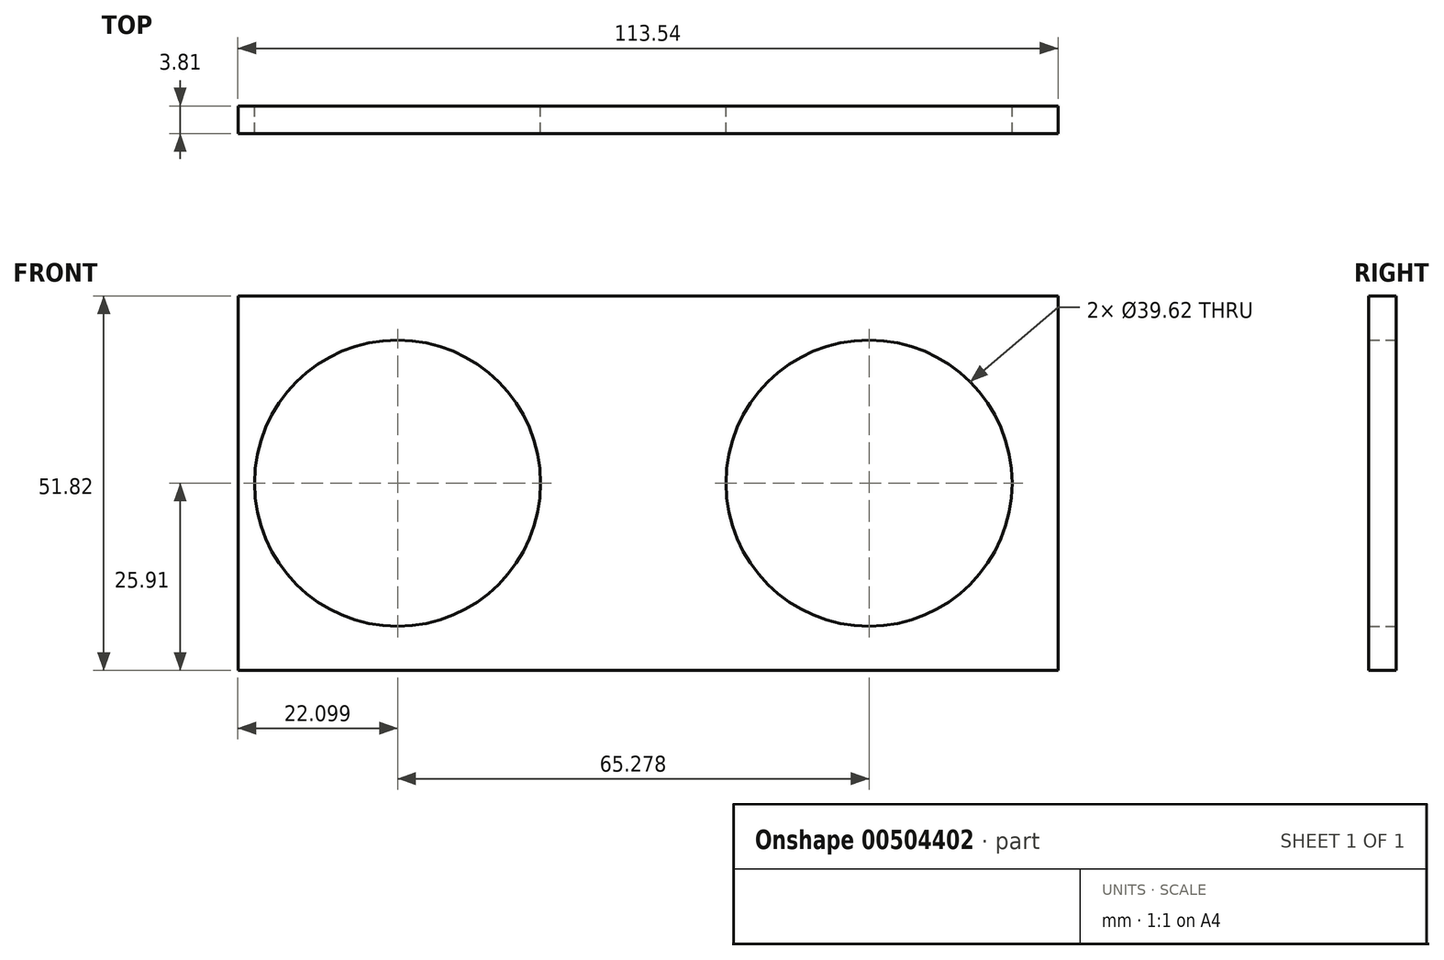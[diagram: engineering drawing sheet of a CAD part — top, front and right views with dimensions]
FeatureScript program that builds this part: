
annotation { "Feature Type Name" : "Feature", "Feature Type Description" : "" }
export const myFeature = defineFeature(function(context is Context, id is Id, definition is map)
    precondition{}
    {
        {
            var Q0;
            Q0=qCreatedBy(makeId("Front.planeOp"),FACE);
            var sketch = newSketch(context, id + "F0", { "sketchPlane" : qUnion([Q0])});
            skLineSegment(sketch, "E0.bottom", {"start": v(-56.77, -25.9) * mm, "end": v(56.77, -25.9) * mm});
            skLineSegment(sketch, "E0.top", {"start": v(-56.77, 25.9) * mm, "end": v(56.77, 25.9) * mm});
            skLineSegment(sketch, "E0.left", {"start": v(-56.77, -25.9) * mm, "end": v(-56.77, 25.9) * mm});
            skLineSegment(sketch, "E0.right", {"start": v(56.77, -25.9) * mm, "end": v(56.77, 25.9) * mm});
            skPoint(sketch, "E0.middle", {"position": v(0, 0) * mm});
            skCircle(sketch, "E1", {"center": v(-34.67, 0) * mm, "radius": 19.81 * mm});
            skLineSegment(sketch, "E2", {"start": v(-54.48, 0) * mm, "end": v(-14.86, 0) * mm});
            skPoint(sketch, "E2.startSnap0", {"position": v(-56.77, 0) * mm});
            skCircle(sketch, "E3", {"center": v(30.6, 0) * mm, "radius": 19.81 * mm});
            skLineSegment(sketch, "E4", {"start": v(10.8, 0) * mm, "end": v(50.42, 0) * mm});
            skLineSegment(sketch, "E5", {"start": v(-56.77, 0) * mm, "end": v(-54.48, 0) * mm});
            skLineSegment(sketch, "E6", {"start": v(56.77, 0) * mm, "end": v(50.42, 0) * mm});
            skSolve(sketch);
        }
        {
            var Q0;
            {var subQ3=sQuery(id+"F0.wireOp",EDGE,"E0.bottom");Q0=makeQuery(id+"F0.imprint","IMPRINT",FACE,{"disambiguationData":[TD([[makeQuery(id+"F0.imprint","IMPRINT",EDGE,{"derivedFrom":subQ3}),1.0]])]});}
            extrude(context, id + "F1", {"entities" : qUnion([Q0]), "depth" : 3.8 * mm});
        }
    });
